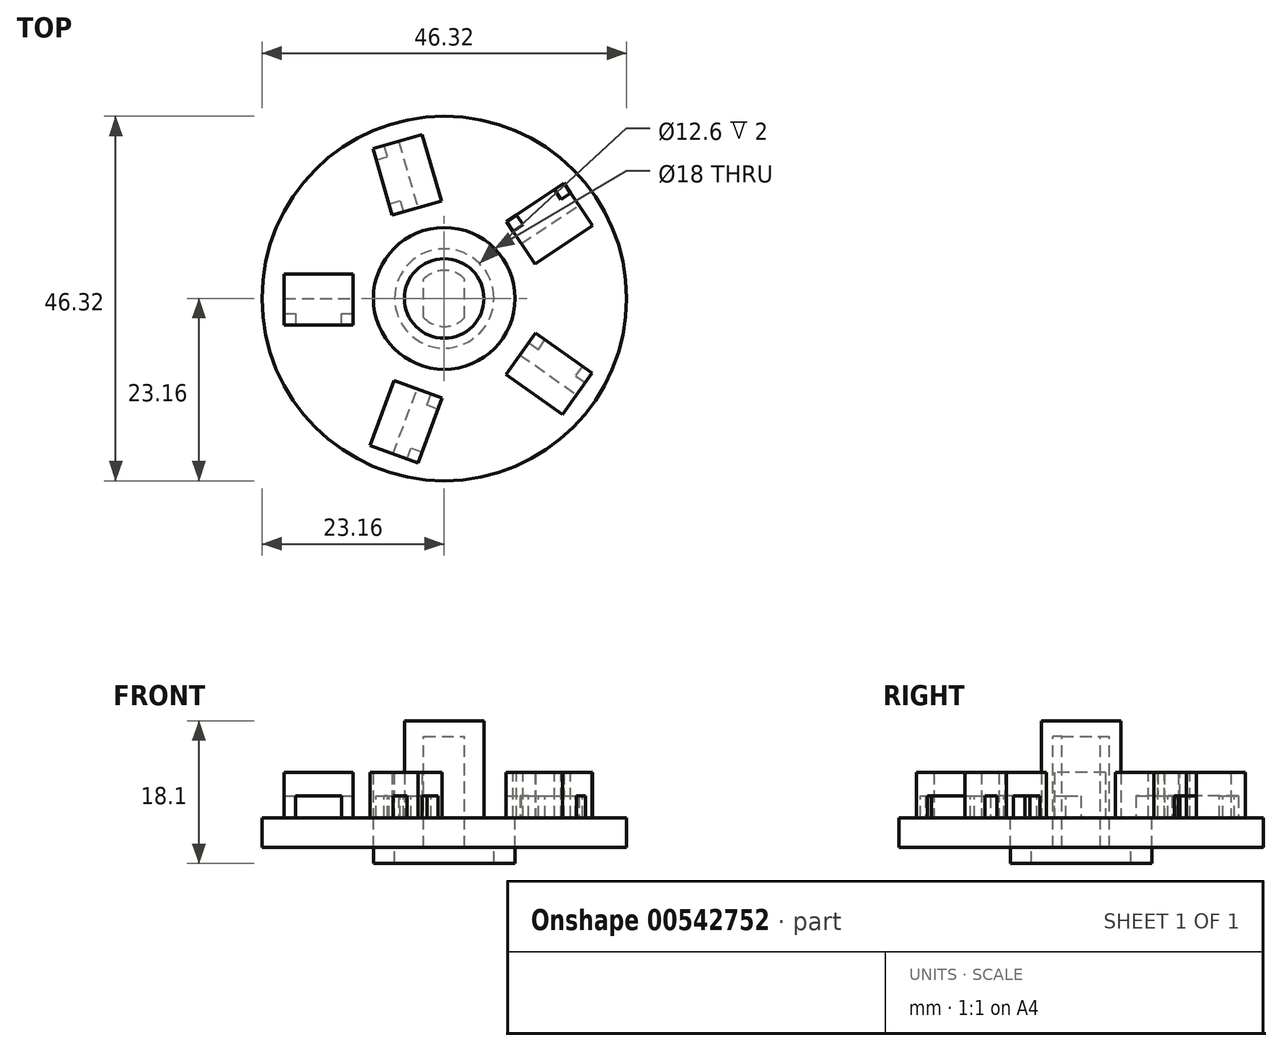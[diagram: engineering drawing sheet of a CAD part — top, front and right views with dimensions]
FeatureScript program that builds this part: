
annotation { "Feature Type Name" : "Feature", "Feature Type Description" : "" }
export const myFeature = defineFeature(function(context is Context, id is Id, definition is map)
    precondition{}
    {
        {
            var Q0;
            Q0=qCreatedBy(makeId("Top.planeOp"),FACE);
            var sketch = newSketch(context, id + "F0", { "sketchPlane" : qUnion([Q0])});
            skCircle(sketch, "E0", {"center": v(0, 0) * mm, "radius": 23.16 * mm});
            skCircle(sketch, "E1", {"center": v(0, 0) * mm, "radius": 6.3 * mm});
            skCircle(sketch, "E2", {"center": v(0, 0) * mm, "radius": 9 * mm});
            skCircle(sketch, "E3", {"center": v(0, 0) * mm, "radius": 5.05 * mm});
            skLineSegment(sketch, "E4", {"start": v(-3.45, -11.5) * mm, "end": v(-6.51, -19.74) * mm});
            skLineSegment(sketch, "E5", {"start": v(-6.51, -19.74) * mm, "end": v(-1.54, -21.59) * mm});
            skLineSegment(sketch, "E6", {"start": v(-1.54, -21.59) * mm, "end": v(1.52, -13.34) * mm});
            skLineSegment(sketch, "E7", {"start": v(1.52, -13.34) * mm, "end": v(-3.45, -11.5) * mm});
            skLineSegment(sketch, "E8", {"start": v(-11.56, 0) * mm, "end": v(-20.36, 0) * mm});
            skLineSegment(sketch, "E9", {"start": v(-20.36, 0) * mm, "end": v(-20.36, -5.3) * mm});
            skLineSegment(sketch, "E10", {"start": v(-20.36, -5.3) * mm, "end": v(-11.56, -5.3) * mm});
            skLineSegment(sketch, "E11", {"start": v(-11.56, -5.3) * mm, "end": v(-11.56, 0) * mm});
            skLineSegment(sketch, "E12", {"start": v(9.63, -7.16) * mm, "end": v(16.82, -12.24) * mm});
            skLineSegment(sketch, "E13", {"start": v(16.82, -12.24) * mm, "end": v(19.88, -7.91) * mm});
            skLineSegment(sketch, "E14", {"start": v(19.88, -7.91) * mm, "end": v(12.7, -2.83) * mm});
            skLineSegment(sketch, "E15", {"start": v(12.7, -2.83) * mm, "end": v(9.63, -7.16) * mm});
            skLineSegment(sketch, "E16", {"start": v(9.78, 6.95) * mm, "end": v(17.11, 11.82) * mm});
            skLineSegment(sketch, "E17", {"start": v(17.11, 11.82) * mm, "end": v(14.18, 16.23) * mm});
            skLineSegment(sketch, "E18", {"start": v(14.18, 16.23) * mm, "end": v(6.85, 11.36) * mm});
            skLineSegment(sketch, "E19", {"start": v(6.85, 11.36) * mm, "end": v(9.78, 6.95) * mm});
            skLineSegment(sketch, "E20", {"start": v(-3.35, 11.52) * mm, "end": v(-5.8, 19.98) * mm});
            skLineSegment(sketch, "E21", {"start": v(-5.8, 19.98) * mm, "end": v(-10.88, 18.5) * mm});
            skLineSegment(sketch, "E22", {"start": v(-10.88, 18.5) * mm, "end": v(-8.44, 10.05) * mm});
            skLineSegment(sketch, "E23", {"start": v(-8.44, 10.05) * mm, "end": v(-3.35, 11.52) * mm});
            skLineSegment(sketch, "E24", {"start": v(-3.35, 11.52) * mm, "end": v(-0.37, 12.38) * mm});
            skLineSegment(sketch, "E25", {"start": v(-0.37, 12.38) * mm, "end": v(-2.82, 20.84) * mm});
            skLineSegment(sketch, "E26", {"start": v(-2.82, 20.84) * mm, "end": v(-5.8, 19.98) * mm});
            skLineSegment(sketch, "E27", {"start": v(-5.8, 19.98) * mm, "end": v(-9.25, 18.98) * mm});
            skPoint(sketch, "E27.endSnap0", {"position": v(-9.25, 18.98) * mm});
            skLineSegment(sketch, "E28", {"start": v(-9.25, 18.98) * mm, "end": v(-6.8, 10.52) * mm});
            skLineSegment(sketch, "E29", {"start": v(-6.8, 10.52) * mm, "end": v(-3.35, 11.52) * mm});
            skLineSegment(sketch, "E30", {"start": v(17.11, 11.82) * mm, "end": v(18.83, 9.24) * mm});
            skLineSegment(sketch, "E31", {"start": v(18.83, 9.24) * mm, "end": v(11.5, 4.37) * mm});
            skLineSegment(sketch, "E32", {"start": v(11.5, 4.37) * mm, "end": v(9.78, 6.95) * mm});
            skLineSegment(sketch, "E33", {"start": v(9.63, -7.16) * mm, "end": v(7.84, -9.69) * mm});
            skLineSegment(sketch, "E34", {"start": v(7.84, -9.69) * mm, "end": v(15.03, -14.77) * mm});
            skLineSegment(sketch, "E35", {"start": v(15.03, -14.77) * mm, "end": v(16.82, -12.24) * mm});
            skLineSegment(sketch, "E36", {"start": v(-3.45, -11.5) * mm, "end": v(-6.36, -10.42) * mm});
            skLineSegment(sketch, "E37", {"start": v(-6.36, -10.42) * mm, "end": v(-9.42, -18.67) * mm});
            skLineSegment(sketch, "E38", {"start": v(-9.42, -18.67) * mm, "end": v(-6.51, -19.74) * mm});
            skLineSegment(sketch, "E39", {"start": v(-11.56, 0) * mm, "end": v(-11.56, 3.1) * mm});
            skLineSegment(sketch, "E40", {"start": v(-11.56, 3.1) * mm, "end": v(-20.36, 3.1) * mm});
            skLineSegment(sketch, "E41", {"start": v(-20.36, 3.1) * mm, "end": v(-20.36, 0) * mm});
            skLineSegment(sketch, "E42.left", {"start": v(2.6, -2.45) * mm, "end": v(2.6, 2.45) * mm});
            skLineSegment(sketch, "E42.right", {"start": v(-2.6, -2.45) * mm, "end": v(-2.6, 2.45) * mm});
            skArc(sketch, "E43", {"start": v(0, -3.57) * mm, "mid": v(1.42, -3.28) * mm, "end": v(2.6, -2.45) * mm});
            skArc(sketch, "E44", {"start": v(0, -3.57) * mm, "mid": v(-1.42, -3.28) * mm, "end": v(-2.6, -2.45) * mm});
            skArc(sketch, "E45", {"start": v(0, 3.57) * mm, "mid": v(1.42, 3.28) * mm, "end": v(2.6, 2.45) * mm});
            skArc(sketch, "E46", {"start": v(0, 3.57) * mm, "mid": v(-1.42, 3.28) * mm, "end": v(-2.6, 2.45) * mm});
            skPoint(sketch, "E47.orphan", {"position": v(2.6, -3.57) * mm});
            skPoint(sketch, "E48.orphan", {"position": v(2.6, 3.57) * mm});
            skPoint(sketch, "E49.orphan", {"position": v(-2.6, 3.57) * mm});
            skPoint(sketch, "E42.bottom.end.orphan", {"position": v(-2.6, -3.57) * mm});
            skSolve(sketch);
        }
        {
            var Q0;
            Q0 = qSketchRegion(id + "F0", true);
            extrude(context, id + "F1", {"entities" : qUnion([Q0]), "oppositeDirection" : true, "depth" : 3.75 * mm, "offsetDistance" : 25 * mm});
        }
        {
            var Q0;
            Q0=makeQuery(id+"F0.imprint","IMPRINT",FACE,{"disambiguationData":[TD([[makeQuery(id+"F0.imprint","IMPRINT",EDGE,{"derivedFrom":sQuery(id+"F0.wireOp",EDGE,"E1")}),-1.0]])]});
            extrude(context, id + "F2", {"entities" : qUnion([Q0]), "oppositeDirection" : true, "depth" : 5.75 * mm, "offsetDistance" : 25 * mm});
        }
        {
            var Q0;
            Q0=makeQuery(id+"F0.imprint","IMPRINT",FACE,{"disambiguationData":[TD([[makeQuery(id+"F0.imprint","IMPRINT",EDGE,{"derivedFrom":sQuery(id+"F0.wireOp",EDGE,"E20")}),-1.0]])]});
            extrude(context, id + "F3", {"entities" : qUnion([Q0]), "depth" : 5.8 * mm, "offsetDistance" : 25 * mm});
        }
        {
            var Q0;
            Q0=makeQuery(id+"F0.imprint","IMPRINT",FACE,{"disambiguationData":[TD([[makeQuery(id+"F0.imprint","IMPRINT",EDGE,{"derivedFrom":sQuery(id+"F0.wireOp",EDGE,"E20")}),-1.0]])]});
            extrude(context, id + "F4", {"entities" : qUnion([Q0]), "operationType" : NewBodyOperationType.ADD, "oppositeDirection" : true, "depth" : 3.75 * mm, "offsetDistance" : 25 * mm});
        }
        {
            var Q0;
            Q0=makeQuery(id+"F3.opExtrude","SWEPT_FACE",FACE,{"disambiguationData":[OSD([sQuery(id+"F0.wireOp",EDGE,"E20")])]});
            var sketch = newSketch(context, id + "F5", { "sketchPlane" : qUnion([Q0])});
            skLineSegment(sketch, "E50.bottom", {"start": v(-20.8, 5.8) * mm, "end": v(-12, 5.8) * mm});
            skLineSegment(sketch, "E50.top", {"start": v(-20.8, 2.8) * mm, "end": v(-12, 2.8) * mm});
            skLineSegment(sketch, "E50.left", {"start": v(-20.8, 5.8) * mm, "end": v(-20.8, 2.8) * mm});
            skLineSegment(sketch, "E50.right", {"start": v(-12, 5.8) * mm, "end": v(-12, 2.8) * mm});
            skSolve(sketch);
        }
        {
            var Q0;
            Q0=makeQuery(id+"F5.imprint","IMPRINT",FACE,{"disambiguationData":[TD([[makeQuery(id+"F5.imprint","IMPRINT",EDGE,{"derivedFrom":sQuery(id+"F5.wireOp",EDGE,"E50.bottom")}),1.0]])]});
            extrude(context, id + "F6", {"entities" : qUnion([Q0]), "operationType" : NewBodyOperationType.ADD, "depth" : 3.4 * mm, "offsetDistance" : 25 * mm});
        }
        {
            var Q0;
            Q0=makeQuery(id+"F0.imprint","IMPRINT",FACE,{"disambiguationData":[TD([[makeQuery(id+"F0.imprint","IMPRINT",EDGE,{"derivedFrom":sQuery(id+"F0.wireOp",EDGE,"E8")}),-1.0]])]});
            var Q1;
            Q1=makeQuery(id+"F0.imprint","IMPRINT",FACE,{"disambiguationData":[TD([[makeQuery(id+"F0.imprint","IMPRINT",EDGE,{"derivedFrom":sQuery(id+"F0.wireOp",EDGE,"E16")}),-1.0]])]});
            var Q2;
            Q2=makeQuery(id+"F0.imprint","IMPRINT",FACE,{"disambiguationData":[TD([[makeQuery(id+"F0.imprint","IMPRINT",EDGE,{"derivedFrom":sQuery(id+"F0.wireOp",EDGE,"E12")}),-1.0]])]});
            var Q3;
            Q3=makeQuery(id+"F0.imprint","IMPRINT",FACE,{"disambiguationData":[TD([[makeQuery(id+"F0.imprint","IMPRINT",EDGE,{"derivedFrom":sQuery(id+"F0.wireOp",EDGE,"E4")}),-1.0]])]});
            extrude(context, id + "F7", {"entities" : qUnion([Q0, Q1, Q2, Q3]), "operationType" : NewBodyOperationType.ADD, "depth" : 5.8 * mm, "offsetDistance" : 25 * mm});
        }
        {
            var Q0;
            Q0=makeQuery(id+"F7.opExtrude","SWEPT_FACE",FACE,{"disambiguationData":[OSD([sQuery(id+"F0.wireOp",EDGE,"E8")])]});
            var sketch = newSketch(context, id + "F8", { "sketchPlane" : qUnion([Q0])});
            skLineSegment(sketch, "E51", {"start": v(-20.36, 5.8) * mm, "end": v(-20.36, 2.8) * mm});
            skLineSegment(sketch, "E52", {"start": v(-20.36, 2.8) * mm, "end": v(-11.56, 2.8) * mm});
            skLineSegment(sketch, "E53", {"start": v(-11.56, 2.8) * mm, "end": v(-11.56, 5.8) * mm});
            skSolve(sketch);
        }
        {
            var Q0;
            Q0=makeQuery(id+"F8.imprint","IMPRINT",FACE,{"disambiguationData":[TD([[makeQuery(id+"F8.imprint","IMPRINT",EDGE,{"derivedFrom":sQuery(id+"F8.wireOp",EDGE,"E51")}),1.0]])]});
            extrude(context, id + "F9", {"entities" : qUnion([Q0]), "operationType" : NewBodyOperationType.ADD, "depth" : 3.4 * mm, "offsetDistance" : 25 * mm});
        }
        {
            var Q0;
            Q0=makeQuery(id+"F7.opExtrude","SWEPT_FACE",FACE,{"disambiguationData":[OSD([sQuery(id+"F0.wireOp",EDGE,"E4")])]});
            var sketch = newSketch(context, id + "F10", { "sketchPlane" : qUnion([Q0])});
            skLineSegment(sketch, "E54", {"start": v(-20.78, 5.8) * mm, "end": v(-20.78, 2.8) * mm});
            skLineSegment(sketch, "E55", {"start": v(-20.78, 2.8) * mm, "end": v(-11.98, 2.8) * mm});
            skLineSegment(sketch, "E56", {"start": v(-11.98, 2.8) * mm, "end": v(-11.98, 5.8) * mm});
            skSolve(sketch);
        }
        {
            var Q0;
            Q0=makeQuery(id+"F10.imprint","IMPRINT",FACE,{"disambiguationData":[TD([[makeQuery(id+"F10.imprint","IMPRINT",EDGE,{"derivedFrom":sQuery(id+"F10.wireOp",EDGE,"E54")}),1.0]])]});
            extrude(context, id + "F11", {"entities" : qUnion([Q0]), "operationType" : NewBodyOperationType.ADD, "depth" : 3.4 * mm, "offsetDistance" : 25 * mm});
        }
        {
            var Q0;
            Q0=makeQuery(id+"F0.imprint","IMPRINT",FACE,{"disambiguationData":[TD([[makeQuery(id+"F0.imprint","IMPRINT",EDGE,{"derivedFrom":sQuery(id+"F0.wireOp",EDGE,"E8")}),-1.0]])]});
            var Q1;
            Q1=makeQuery(id+"F0.imprint","IMPRINT",FACE,{"disambiguationData":[TD([[makeQuery(id+"F0.imprint","IMPRINT",EDGE,{"derivedFrom":sQuery(id+"F0.wireOp",EDGE,"E4")}),-1.0]])]});
            var Q2;
            Q2=makeQuery(id+"F0.imprint","IMPRINT",FACE,{"disambiguationData":[TD([[makeQuery(id+"F0.imprint","IMPRINT",EDGE,{"derivedFrom":sQuery(id+"F0.wireOp",EDGE,"E16")}),-1.0]])]});
            var Q3;
            Q3=makeQuery(id+"F0.imprint","IMPRINT",FACE,{"disambiguationData":[TD([[makeQuery(id+"F0.imprint","IMPRINT",EDGE,{"derivedFrom":sQuery(id+"F0.wireOp",EDGE,"E12")}),-1.0]])]});
            extrude(context, id + "F12", {"entities" : qUnion([Q0, Q1, Q2, Q3]), "oppositeDirection" : true, "depth" : 3.75 * mm, "offsetDistance" : 25 * mm});
        }
        {
            var Q0;
            Q0=makeQuery(id+"F7.opExtrude","SWEPT_FACE",FACE,{"disambiguationData":[OSD([sQuery(id+"F0.wireOp",EDGE,"E12")])]});
            var sketch = newSketch(context, id + "F13", { "sketchPlane" : qUnion([Q0])});
            skLineSegment(sketch, "E57", {"start": v(-12, 5.8) * mm, "end": v(-12, 2.8) * mm});
            skLineSegment(sketch, "E58", {"start": v(-12, 2.8) * mm, "end": v(-20.8, 2.8) * mm});
            skLineSegment(sketch, "E59", {"start": v(-20.8, 2.8) * mm, "end": v(-20.8, 5.8) * mm});
            skSolve(sketch);
        }
        {
            var Q0;
            Q0=makeQuery(id+"F13.imprint","IMPRINT",FACE,{"disambiguationData":[TD([[makeQuery(id+"F13.imprint","IMPRINT",EDGE,{"derivedFrom":sQuery(id+"F13.wireOp",EDGE,"E57")}),-1.0]])]});
            extrude(context, id + "F14", {"entities" : qUnion([Q0]), "operationType" : NewBodyOperationType.ADD, "depth" : 3.4 * mm, "offsetDistance" : 25 * mm});
        }
        {
            var Q0;
            Q0=makeQuery(id+"F7.opExtrude","SWEPT_FACE",FACE,{"disambiguationData":[OSD([sQuery(id+"F0.wireOp",EDGE,"E16")])]});
            var sketch = newSketch(context, id + "F15", { "sketchPlane" : qUnion([Q0])});
            skLineSegment(sketch, "E60", {"start": v(-12, 5.8) * mm, "end": v(-12, 2.8) * mm});
            skLineSegment(sketch, "E61", {"start": v(-12, 2.8) * mm, "end": v(-20.8, 2.8) * mm});
            skLineSegment(sketch, "E62", {"start": v(-20.8, 2.8) * mm, "end": v(-20.8, 5.8) * mm});
            skSolve(sketch);
        }
        {
            var Q0;
            Q0=makeQuery(id+"F15.imprint","IMPRINT",FACE,{"disambiguationData":[TD([[makeQuery(id+"F15.imprint","IMPRINT",EDGE,{"derivedFrom":sQuery(id+"F15.wireOp",EDGE,"E60")}),-1.0]])]});
            extrude(context, id + "F16", {"entities" : qUnion([Q0]), "operationType" : NewBodyOperationType.ADD, "depth" : 3.4 * mm, "offsetDistance" : 25 * mm});
        }
        {
            var Q0;
            Q0=makeQuery(id+"F0.imprint","IMPRINT",FACE,{"disambiguationData":[TD([[makeQuery(id+"F0.imprint","IMPRINT",EDGE,{"derivedFrom":sQuery(id+"F0.wireOp",EDGE,"E1")}),1.0]])]});
            extrude(context, id + "F17", {"entities" : qUnion([Q0]), "operationType" : NewBodyOperationType.ADD, "oppositeDirection" : true, "depth" : 3.75 * mm, "offsetDistance" : 25 * mm});
        }
        {
            var Q0;
            Q0=makeQuery(id+"F0.imprint","IMPRINT",FACE,{"disambiguationData":[TD([[makeQuery(id+"F0.imprint","IMPRINT",EDGE,{"derivedFrom":sQuery(id+"F0.wireOp",EDGE,"E3")}),1.0]])]});
            extrude(context, id + "F18", {"entities" : qUnion([Q0]), "operationType" : NewBodyOperationType.ADD, "oppositeDirection" : true, "depth" : 3.75 * mm, "offsetDistance" : 25 * mm});
        }
        {
            var Q0;
            Q0=makeQuery(id+"F0.imprint","IMPRINT",FACE,{"disambiguationData":[TD([[makeQuery(id+"F0.imprint","IMPRINT",EDGE,{"derivedFrom":sQuery(id+"F0.wireOp",EDGE,"E3")}),1.0]])]});
            extrude(context, id + "F19", {"entities" : qUnion([Q0]), "operationType" : NewBodyOperationType.ADD, "depth" : 10.35 * mm, "offsetDistance" : 25 * mm});
        }
        {
            var Q0;
            Q0=makeQuery(id+"F19.opExtrude","CAP_FACE",FACE,{"disambiguationData":[OSD([sQuery(id+"F0.wireOp",EDGE,"E3"),sQuery(id+"F0.wireOp",EDGE,"E42.left"),sQuery(id+"F0.wireOp",EDGE,"E42.right"),sQuery(id+"F0.wireOp",EDGE,"E43"),sQuery(id+"F0.wireOp",EDGE,"E44"),sQuery(id+"F0.wireOp",EDGE,"E45"),sQuery(id+"F0.wireOp",EDGE,"E46")])],"isStart":false});
            var sketch = newSketch(context, id + "F20", { "sketchPlane" : qUnion([Q0])});
            skCircle(sketch, "E63", {"center": v(0, 0) * mm, "radius": 5.05 * mm});
            skSolve(sketch);
        }
        {
            var Q0;
            Q0=makeQuery(id+"F20.imprint","IMPRINT",FACE,{"disambiguationData":[TD([[makeQuery(id+"F20.imprint","IMPRINT",EDGE,{"derivedFrom":sQuery(id+"F20.wireOp",EDGE,"E63")}),1.0]])]});
            var Q1;
            Q1=makeQuery(id+"F20.imprint","IMPRINT",FACE,{"disambiguationData":[TD([[makeQuery(id+"F20.imprint","IMPRINT",EDGE,{"derivedFrom":makeQuery(id+"F19.opExtrude","CAP_EDGE",EDGE,{"disambiguationData":[OSD([sQuery(id+"F0.wireOp",EDGE,"E42.left")])],"isStart":false})}),1.0]])]});
            extrude(context, id + "F21", {"entities" : qUnion([Q0, Q1]), "operationType" : NewBodyOperationType.ADD, "depth" : 2 * mm, "offsetDistance" : 25 * mm});
        }
        {
            var Q0;
            Q0=makeQuery(id+"F0.imprint","IMPRINT",FACE,{"disambiguationData":[TD([[makeQuery(id+"F0.imprint","IMPRINT",EDGE,{"derivedFrom":sQuery(id+"F0.wireOp",EDGE,"E21")}),1.0]])]});
            var Q1;
            Q1=makeQuery(id+"F0.imprint","IMPRINT",FACE,{"disambiguationData":[TD([[makeQuery(id+"F0.imprint","IMPRINT",EDGE,{"derivedFrom":sQuery(id+"F0.wireOp",EDGE,"E20")}),1.0]])]});
            var Q2;
            Q2=makeQuery(id+"F0.imprint","IMPRINT",FACE,{"disambiguationData":[TD([[makeQuery(id+"F0.imprint","IMPRINT",EDGE,{"derivedFrom":sQuery(id+"F0.wireOp",EDGE,"E8")}),1.0]])]});
            var Q3;
            Q3=makeQuery(id+"F0.imprint","IMPRINT",FACE,{"disambiguationData":[TD([[makeQuery(id+"F0.imprint","IMPRINT",EDGE,{"derivedFrom":sQuery(id+"F0.wireOp",EDGE,"E4")}),1.0]])]});
            var Q4;
            Q4=makeQuery(id+"F0.imprint","IMPRINT",FACE,{"disambiguationData":[TD([[makeQuery(id+"F0.imprint","IMPRINT",EDGE,{"derivedFrom":sQuery(id+"F0.wireOp",EDGE,"E12")}),1.0]])]});
            var Q5;
            Q5=makeQuery(id+"F0.imprint","IMPRINT",FACE,{"disambiguationData":[TD([[makeQuery(id+"F0.imprint","IMPRINT",EDGE,{"derivedFrom":sQuery(id+"F0.wireOp",EDGE,"E16")}),1.0]])]});
            extrude(context, id + "F22", {"entities" : qUnion([Q0, Q1, Q2, Q3, Q4, Q5]), "operationType" : NewBodyOperationType.ADD, "oppositeDirection" : true, "depth" : 3.75 * mm, "offsetDistance" : 25 * mm});
        }
        {
            var Q0;
            {var subQ0=sQuery(id+"F0.wireOp",EDGE,"E16");Q0=makeQuery(id+"F16.boolean.opBoolean","MERGE",FACE,{"derivedFrom":[makeQuery(id+"F7.opExtrude","CAP_FACE",FACE,{"disambiguationData":[OSD([subQ0,sQuery(id+"F0.wireOp",EDGE,"E30"),sQuery(id+"F0.wireOp",EDGE,"E31"),sQuery(id+"F0.wireOp",EDGE,"E32")])],"isStart":false}),makeQuery(id+"F16.opExtrude","SWEPT_FACE",FACE,{"disambiguationData":[OSD([subQ0])]})]});}
            var sketch = newSketch(context, id + "F23", { "sketchPlane" : qUnion([Q0])});
            skLineSegment(sketch, "E64", {"start": v(16.06, 13.4) * mm, "end": v(14.81, 12.57) * mm});
            skLineSegment(sketch, "E65", {"start": v(14.81, 12.57) * mm, "end": v(13.98, 13.82) * mm});
            skLineSegment(sketch, "E66", {"start": v(8.73, 8.53) * mm, "end": v(9.98, 9.36) * mm});
            skLineSegment(sketch, "E67", {"start": v(9.98, 9.36) * mm, "end": v(9.15, 10.6) * mm});
            skSolve(sketch);
        }
        {
            var Q0;
            {var subQ0=sQuery(id+"F23.wireOp",EDGE,"E64");Q0=makeQuery(id+"F23.imprint","IMPRINT",FACE,{"disambiguationData":[TD([[makeQuery(id+"F23.imprint","IMPRINT",EDGE,{"derivedFrom":subQ0}),-1.0]])]});}
            var Q1;
            {var subQ0=sQuery(id+"F23.wireOp",EDGE,"E66");Q1=makeQuery(id+"F23.imprint","IMPRINT",FACE,{"disambiguationData":[TD([[makeQuery(id+"F23.imprint","IMPRINT",EDGE,{"derivedFrom":subQ0}),1.0]])]});}
            extrude(context, id + "F24", {"entities" : qUnion([Q0, Q1]), "oppositeDirection" : true, "depth" : 5.75 * mm, "offsetDistance" : 25 * mm});
        }
        {
            var Q0;
            {var subQ0=sQuery(id+"F0.wireOp",EDGE,"E12");Q0=makeQuery(id+"F14.boolean.opBoolean","MERGE",FACE,{"derivedFrom":[makeQuery(id+"F7.opExtrude","CAP_FACE",FACE,{"disambiguationData":[OSD([subQ0,sQuery(id+"F0.wireOp",EDGE,"E33"),sQuery(id+"F0.wireOp",EDGE,"E34"),sQuery(id+"F0.wireOp",EDGE,"E35")])],"isStart":false}),makeQuery(id+"F14.opExtrude","SWEPT_FACE",FACE,{"disambiguationData":[OSD([subQ0])]})]});}
            var sketch = newSketch(context, id + "F25", { "sketchPlane" : qUnion([Q0])});
            skLineSegment(sketch, "E68", {"start": v(17.91, -10.69) * mm, "end": v(16.69, -9.82) * mm});
            skLineSegment(sketch, "E69", {"start": v(16.69, -9.82) * mm, "end": v(17.56, -8.6) * mm});
            skLineSegment(sketch, "E70", {"start": v(12.82, -5.25) * mm, "end": v(11.95, -6.47) * mm});
            skLineSegment(sketch, "E71", {"start": v(11.95, -6.47) * mm, "end": v(10.73, -5.6) * mm});
            skSolve(sketch);
        }
        {
            var Q0;
            {var subQ0=sQuery(id+"F25.wireOp",EDGE,"E68");Q0=makeQuery(id+"F25.imprint","IMPRINT",FACE,{"disambiguationData":[TD([[makeQuery(id+"F25.imprint","IMPRINT",EDGE,{"derivedFrom":subQ0}),-1.0]])]});}
            var Q1;
            {var subQ0=sQuery(id+"F25.wireOp",EDGE,"E70");Q1=makeQuery(id+"F25.imprint","IMPRINT",FACE,{"disambiguationData":[TD([[makeQuery(id+"F25.imprint","IMPRINT",EDGE,{"derivedFrom":subQ0}),-1.0]])]});}
            extrude(context, id + "F26", {"entities" : qUnion([Q0, Q1]), "operationType" : NewBodyOperationType.ADD, "oppositeDirection" : true, "depth" : 5.75 * mm, "offsetDistance" : 25 * mm});
        }
        {
            var Q0;
            {var subQ0=sQuery(id+"F0.wireOp",EDGE,"E4");Q0=makeQuery(id+"F11.boolean.opBoolean","MERGE",FACE,{"derivedFrom":[makeQuery(id+"F7.opExtrude","CAP_FACE",FACE,{"disambiguationData":[OSD([subQ0,sQuery(id+"F0.wireOp",EDGE,"E36"),sQuery(id+"F0.wireOp",EDGE,"E37"),sQuery(id+"F0.wireOp",EDGE,"E38")])],"isStart":false}),makeQuery(id+"F11.opExtrude","SWEPT_FACE",FACE,{"disambiguationData":[OSD([subQ0])]})]});}
            var sketch = newSketch(context, id + "F27", { "sketchPlane" : qUnion([Q0])});
            skLineSegment(sketch, "E72", {"start": v(-4.73, -20.4) * mm, "end": v(-4.2, -19) * mm});
            skLineSegment(sketch, "E73", {"start": v(-4.2, -19) * mm, "end": v(-2.8, -19.52) * mm});
            skLineSegment(sketch, "E74", {"start": v(-0.79, -14.08) * mm, "end": v(-2.2, -13.56) * mm});
            skLineSegment(sketch, "E75", {"start": v(-2.2, -13.56) * mm, "end": v(-1.67, -12.15) * mm});
            skSolve(sketch);
        }
        {
            var Q0;
            {var subQ0=sQuery(id+"F27.wireOp",EDGE,"E72");Q0=makeQuery(id+"F27.imprint","IMPRINT",FACE,{"disambiguationData":[TD([[makeQuery(id+"F27.imprint","IMPRINT",EDGE,{"derivedFrom":subQ0}),-1.0]])]});}
            var Q1;
            {var subQ0=sQuery(id+"F27.wireOp",EDGE,"E74");Q1=makeQuery(id+"F27.imprint","IMPRINT",FACE,{"disambiguationData":[TD([[makeQuery(id+"F27.imprint","IMPRINT",EDGE,{"derivedFrom":subQ0}),-1.0]])]});}
            extrude(context, id + "F28", {"entities" : qUnion([Q0, Q1]), "operationType" : NewBodyOperationType.ADD, "oppositeDirection" : true, "depth" : 5.75 * mm, "offsetDistance" : 25 * mm});
        }
        {
            var Q0;
            {var subQ0=sQuery(id+"F0.wireOp",EDGE,"E8");Q0=makeQuery(id+"F9.boolean.opBoolean","MERGE",FACE,{"derivedFrom":[makeQuery(id+"F7.opExtrude","CAP_FACE",FACE,{"disambiguationData":[OSD([subQ0,sQuery(id+"F0.wireOp",EDGE,"E39"),sQuery(id+"F0.wireOp",EDGE,"E40"),sQuery(id+"F0.wireOp",EDGE,"E41")])],"isStart":false}),makeQuery(id+"F9.opExtrude","SWEPT_FACE",FACE,{"disambiguationData":[OSD([subQ0])]})]});}
            var sketch = newSketch(context, id + "F29", { "sketchPlane" : qUnion([Q0])});
            skLineSegment(sketch, "E76", {"start": v(-20.36, -1.9) * mm, "end": v(-18.86, -1.9) * mm});
            skLineSegment(sketch, "E77", {"start": v(-18.86, -1.9) * mm, "end": v(-18.86, -3.4) * mm});
            skLineSegment(sketch, "E78", {"start": v(-13.06, -3.4) * mm, "end": v(-13.06, -1.9) * mm});
            skLineSegment(sketch, "E79", {"start": v(-13.06, -1.9) * mm, "end": v(-11.56, -1.9) * mm});
            skSolve(sketch);
        }
        {
            var Q0;
            {var subQ0=sQuery(id+"F29.wireOp",EDGE,"E76");Q0=makeQuery(id+"F29.imprint","IMPRINT",FACE,{"disambiguationData":[TD([[makeQuery(id+"F29.imprint","IMPRINT",EDGE,{"derivedFrom":subQ0}),-1.0]])]});}
            var Q1;
            {var subQ0=sQuery(id+"F29.wireOp",EDGE,"E78");Q1=makeQuery(id+"F29.imprint","IMPRINT",FACE,{"disambiguationData":[TD([[makeQuery(id+"F29.imprint","IMPRINT",EDGE,{"derivedFrom":subQ0}),-1.0]])]});}
            extrude(context, id + "F30", {"entities" : qUnion([Q0, Q1]), "operationType" : NewBodyOperationType.ADD, "oppositeDirection" : true, "depth" : 5.75 * mm, "offsetDistance" : 25 * mm});
        }
        {
            var Q0;
            Q0=makeQuery(id+"F6.boolean.opBoolean","MERGE",FACE,{"derivedFrom":[makeQuery(id+"F3.opExtrude","CAP_FACE",FACE,{"disambiguationData":[OSD([sQuery(id+"F0.wireOp",EDGE,"E20"),sQuery(id+"F0.wireOp",EDGE,"E24"),sQuery(id+"F0.wireOp",EDGE,"E25"),sQuery(id+"F0.wireOp",EDGE,"E26")])],"isStart":false}),makeQuery(id+"F6.opExtrude","SWEPT_FACE",FACE,{"disambiguationData":[OSD([sQuery(id+"F5.wireOp",EDGE,"E50.bottom")])]})]});
            var sketch = newSketch(context, id + "F31", { "sketchPlane" : qUnion([Q0])});
            skLineSegment(sketch, "E80", {"start": v(-7.03, 12.02) * mm, "end": v(-5.6, 12.44) * mm});
            skLineSegment(sketch, "E81", {"start": v(-5.6, 12.44) * mm, "end": v(-5.17, 11) * mm});
            skLineSegment(sketch, "E82", {"start": v(-8.64, 17.6) * mm, "end": v(-7.2, 18) * mm});
            skLineSegment(sketch, "E83", {"start": v(-7.2, 18) * mm, "end": v(-7.62, 19.45) * mm});
            skSolve(sketch);
        }
        {
            var Q0;
            {var subQ0=sQuery(id+"F31.wireOp",EDGE,"E80");Q0=makeQuery(id+"F31.imprint","IMPRINT",FACE,{"disambiguationData":[TD([[makeQuery(id+"F31.imprint","IMPRINT",EDGE,{"derivedFrom":subQ0}),-1.0]])]});}
            var Q1;
            {var subQ0=sQuery(id+"F31.wireOp",EDGE,"E82");Q1=makeQuery(id+"F31.imprint","IMPRINT",FACE,{"disambiguationData":[TD([[makeQuery(id+"F31.imprint","IMPRINT",EDGE,{"derivedFrom":subQ0}),1.0]])]});}
            extrude(context, id + "F32", {"entities" : qUnion([Q0, Q1]), "operationType" : NewBodyOperationType.ADD, "oppositeDirection" : true, "depth" : 5.75 * mm, "offsetDistance" : 25 * mm});
        }
    });
